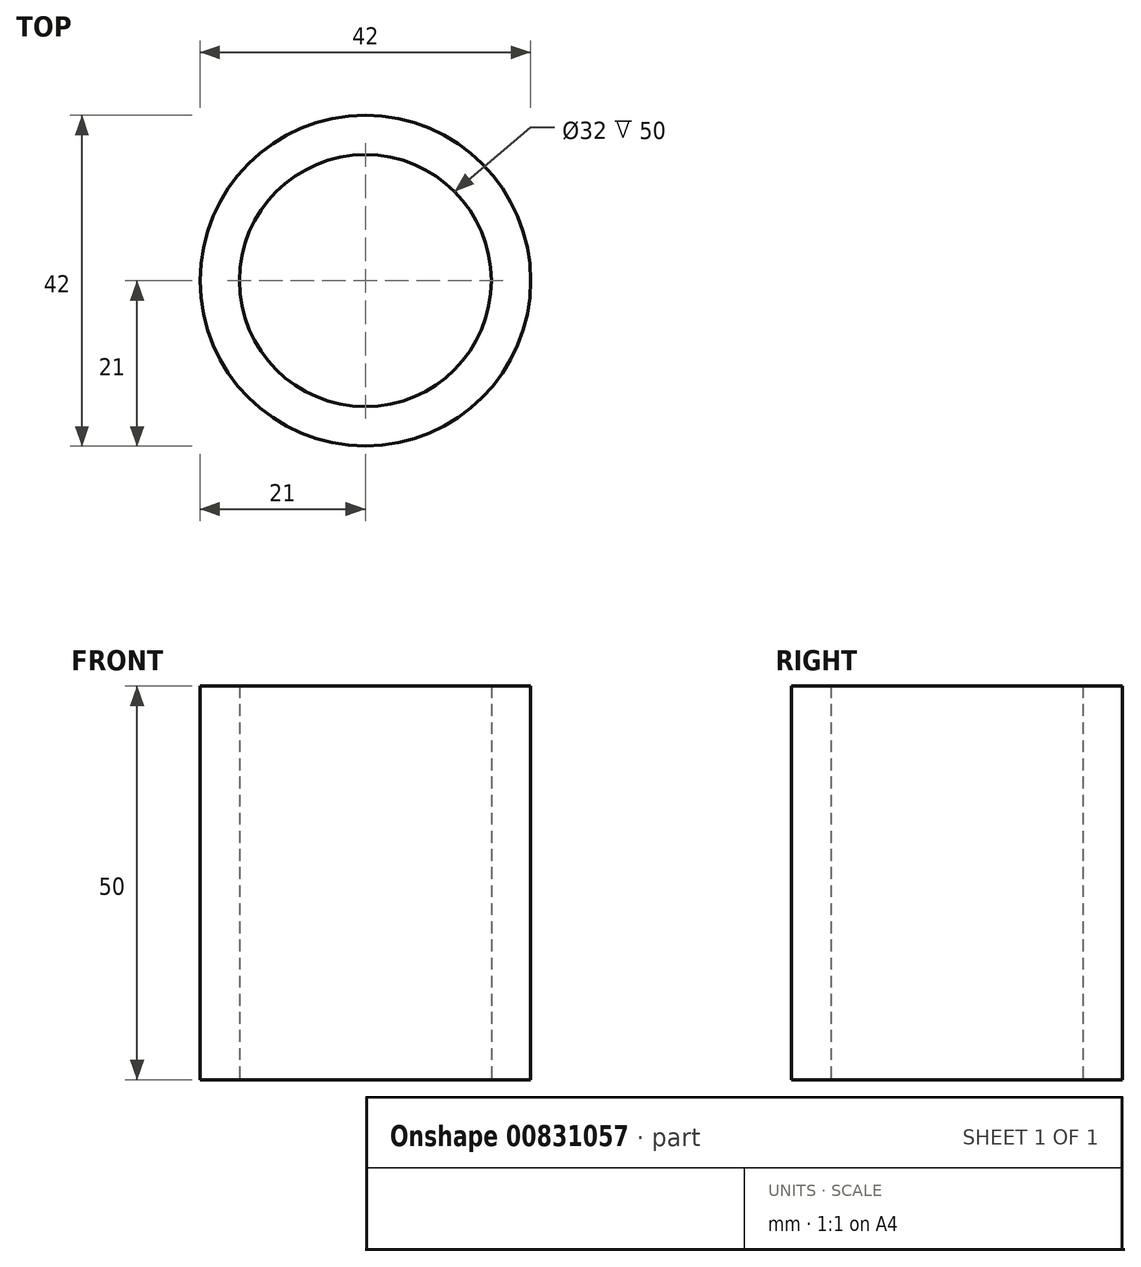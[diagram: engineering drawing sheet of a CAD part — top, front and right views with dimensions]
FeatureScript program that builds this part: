
annotation { "Feature Type Name" : "Feature", "Feature Type Description" : "" }
export const myFeature = defineFeature(function(context is Context, id is Id, definition is map)
    precondition{}
    {
        {
            var Q0;
            Q0=qCreatedBy(makeId("Top.planeOp"),FACE);
            var sketch = newSketch(context, id + "F0", { "sketchPlane" : qUnion([Q0])});
            skCircle(sketch, "E0", {"center": v(0, 0) * mm, "radius": 21 * mm});
            skCircle(sketch, "E1", {"center": v(0, 0) * mm, "radius": 16 * mm});
            skSolve(sketch);
        }
        {
            var Q0;
            Q0=makeQuery(id+"F0.imprint","IMPRINT",FACE,{"disambiguationData":[TD([[makeQuery(id+"F0.imprint","IMPRINT",EDGE,{"derivedFrom":sQuery(id+"F0.wireOp",EDGE,"E0")}),1.0]])]});
            extrude(context, id + "F1", {"entities" : qUnion([Q0]), "depth" : 50 * mm, "offsetDistance" : 25 * mm});
        }
    });
